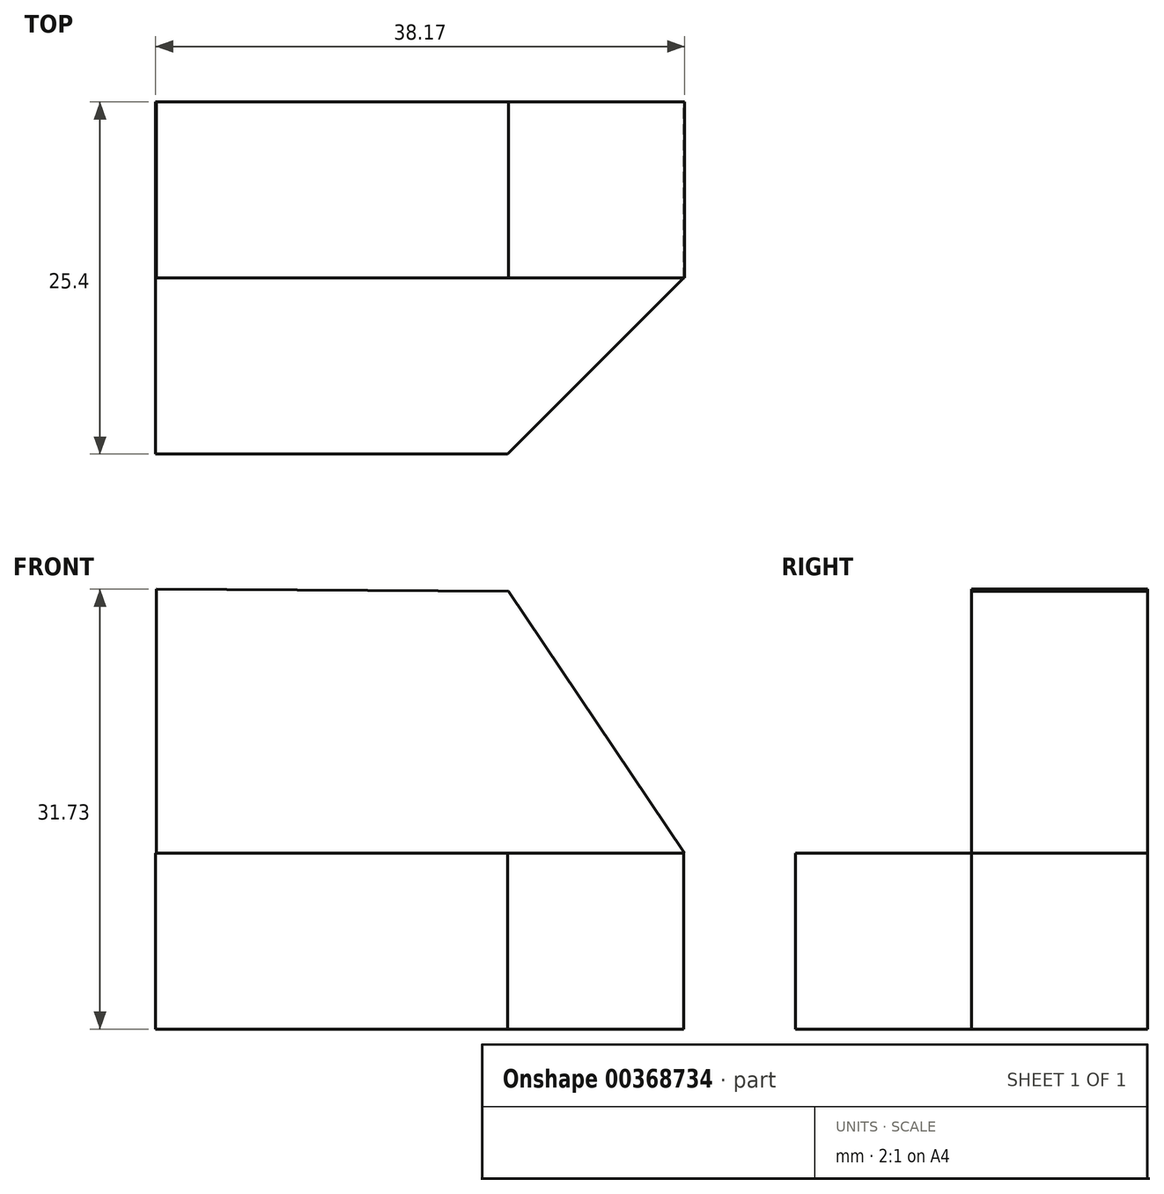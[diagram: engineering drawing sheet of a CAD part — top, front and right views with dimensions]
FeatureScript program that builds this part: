
annotation { "Feature Type Name" : "Feature", "Feature Type Description" : "" }
export const myFeature = defineFeature(function(context is Context, id is Id, definition is map)
    precondition{}
    {
        {
            var Q0;
            Q0=qCreatedBy(makeId("Front.planeOp"),FACE);
            var sketch = newSketch(context, id + "F0", { "sketchPlane" : qUnion([Q0])});
            skLineSegment(sketch, "E0", {"start": v(-25.3, 35.6) * mm, "end": v(-25.3, 16.55) * mm});
            skLineSegment(sketch, "E1", {"start": v(-25.3, 16.55) * mm, "end": v(12.8, 16.55) * mm});
            skLineSegment(sketch, "E2", {"start": v(12.8, 16.55) * mm, "end": v(0.1, 35.44) * mm});
            skLineSegment(sketch, "E3", {"start": v(0.1, 35.44) * mm, "end": v(-25.3, 35.6) * mm});
            skSolve(sketch);
        }
        {
            var Q0;
            Q0=makeQuery(id+"F0.imprint","IMPRINT",FACE,{"disambiguationData":[TD([[makeQuery(id+"F0.imprint","IMPRINT",EDGE,{"derivedFrom":sQuery(id+"F0.wireOp",EDGE,"E0")}),1.0]])]});
            extrude(context, id + "F1", {"entities" : qUnion([Q0]), "depth" : 12.7 * mm});
        }
        {
            var Q0;
            Q0=qCreatedBy(makeId("Front.planeOp"),FACE);
            var sketch = newSketch(context, id + "F2", { "sketchPlane" : qUnion([Q0])});
            skLineSegment(sketch, "E4", {"start": v(12.72, 16.57) * mm, "end": v(12.72, 3.87) * mm});
            skLineSegment(sketch, "E5", {"start": v(12.72, 3.87) * mm, "end": v(-25.38, 3.87) * mm});
            skLineSegment(sketch, "E6", {"start": v(-25.38, 3.87) * mm, "end": v(-25.38, 16.57) * mm});
            skLineSegment(sketch, "E7", {"start": v(-25.38, 16.57) * mm, "end": v(12.72, 16.57) * mm});
            skSolve(sketch);
        }
        {
            var Q0;
            Q0 = qSketchRegion(id + "F2", true);
            extrude(context, id + "F3", {"entities" : qUnion([Q0]), "operationType" : NewBodyOperationType.ADD, "depth" : 25.4 * mm});
        }
        {
            var Q0;
            Q0=makeQuery(id+"F3.opExtrude","CAP_EDGE",EDGE,{"disambiguationData":[OSD([sQuery(id+"F2.wireOp",EDGE,"E4")])],"isStart":false});
            chamfer(context, id + "F4", {"entities" : qUnion([Q0]), "width" : 12.7 * mm, "tangentPropagation" : true});
        }
    });
